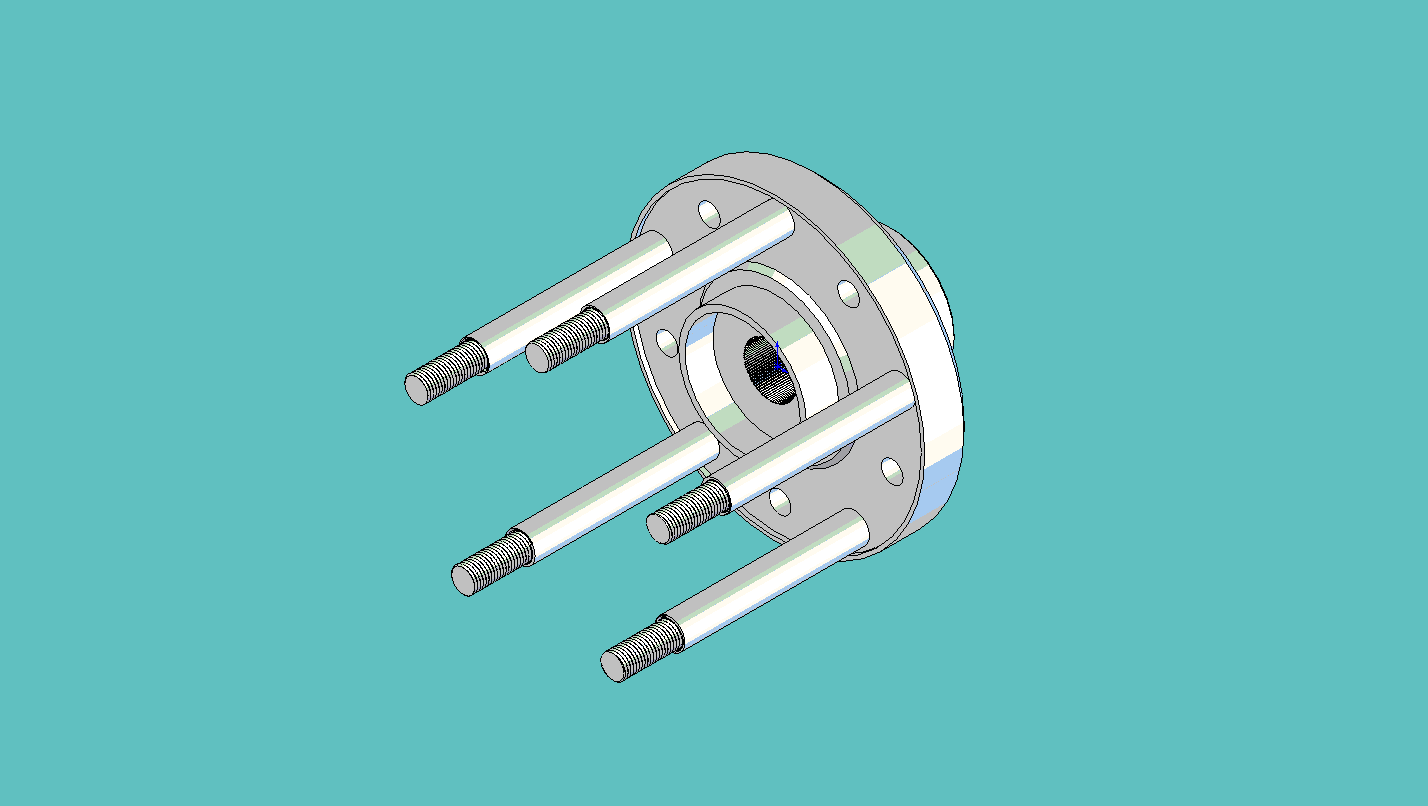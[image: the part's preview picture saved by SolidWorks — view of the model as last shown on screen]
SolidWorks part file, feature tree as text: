
SOLIDWORKS PART (.sldprt)
format: sldprt  version: not decoded by parser v0  size: 2,162,688 bytes
history: native  units: mm
features: sketch x11, cut_extrude x5, extrude x4, chamfer x3, plane x2, material x1, helix x1, sweep x1, pattern_circular x1 (+13 scaffold rows collapsed)
feature tree (42):
  scaffold x13  (default folders/planes/origin — collapsed)
  material  "Material <not specified>"
  sketch  "Sketch1"  dims[D1=165.1mm]
  extrude  "Extrude1"  Depth=1.27mm
  sketch  "Sketch2"  dims[D1=~83.149522mm]
  cut_extrude  "Cut-Extrude1"  Depth=2.54mm
  sketch  "Sketch3"  dims[D1=~70.445004mm]
  chamfer  "Chamfer1"  Distance=2.54mm Angle=45deg
  sketch  "Sketch8"  dims[D1=16.51mm D2=~70.192131mm]
  extrude  "Extrude5"  Depth=101.6mm
  extrude  "Extrude6"  Depth=17.78mm
  sketch  "Sketch9"
  cut_extrude  "Cut-Extrude2"  Depth=15.24mm
  sketch  "Sketch10"
  cut_extrude  "Cut-Extrude3"  Depth=25.4mm
  chamfer  "Chamfer4"  Distance=1.27mm Angle=45deg
  sketch  "Sketch11"
  cut_extrude  "Cut-Extrude4"  [1 undecoded]
  sketch  "Sketch12"
  cut_extrude  "Cut-Extrude5"  [1 undecoded]
  sketch  "Sketch13"  dims[D1=13.97mm]
  extrude  "Extrude7"  Depth=31.75mm
  plane  "Plane1"  Offset=2.54mm
  sketch  "Sketch17"
  helix  "Helix/Spiral1"  Pitch=34.54mm
  plane  "Plane2"  Offset=21.59mm
  sketch  "Sketch18"
  sweep  "Cut-Sweep1"
  pattern_circular  "CirPattern1"  Count=5 Angle=360deg
  chamfer  "Chamfer5"  Distance=5.08mm Angle=45deg
decode coverage: 17 of 26 modeling features carry decoded parameters
note: ~ marks probable driven/reference dimensions
note: 2 parameter values undecoded
note: suppression state not decoded; provenance and decode notes live in map.json
